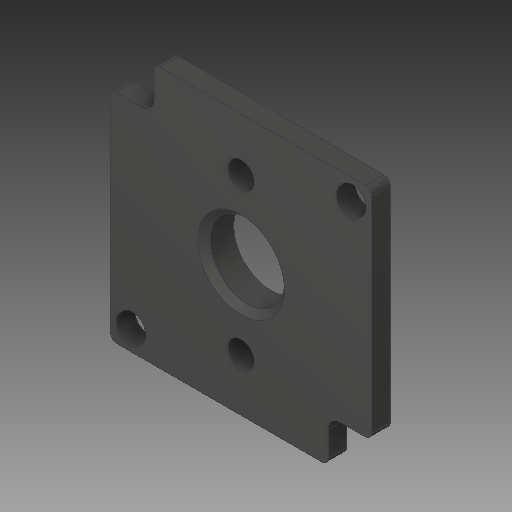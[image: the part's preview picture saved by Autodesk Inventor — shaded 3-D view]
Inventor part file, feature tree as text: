
AUTODESK INVENTOR PART (.ipt)
format: ipt  version: 2017 (Build 210142000, 142)  size: 242,176 bytes
history: native  units: in
note: dims shown in document units (in); Inventor stores cm internally (conversion verified against a paired STEP export)
features: fillet x1
ambient origin geometry x8: Origin, YZ Plane, XZ Plane, XY Plane, X Axis, Y Axis, Z Axis, Center Point
bodies: Solid1 (feature_tree)
feature tree (1):
  fillet  "Fillet4"  [1 undecoded]
note: 1 required parameter value undecoded (feature->parameter linkage not recoverable at this tier; creation-order binding heuristic only, values carry confidence <= 0.55)
